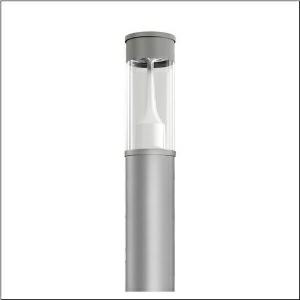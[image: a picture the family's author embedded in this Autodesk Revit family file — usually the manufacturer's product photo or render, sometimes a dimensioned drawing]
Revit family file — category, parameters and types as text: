
# Revit family: city-light_400_iq___p1_0a_5xa5305lf14hp_1a81
name_source: partatom
category: Lighting Fixtures
units: mm (PartAtom-declared; Revit-internal decimal feet)

## family parameters
Cut with Voids When Loaded = No
Host = Face
Light Source = No
Part Type = Normal
Room Calculation Point = No
Round Connector Dimension = Use Diameter
Shared = No

## types (1)
- --- (1 x LED, 4910 lm, 33.6 W, 4000K)
    Apparent Load = 34 VA
    CIE Flux Codes = 31 62 91 95 100
    Color Rendering = 70
    Color Temperature = 4000K
    Default Elevation = 1800 mm
    Description = City-Light 400 iQ, light pillar, Module 540 iQ-SR, primary light control with 3 zone facetted reflector, of plastic, silver coated, highly specular, structured, primary optical cover: cover, of PMMA, transparent, partly coated, light distribution: P1.0a, primary light characteristic: strongly asymmetric, LED, High Power LED, rated luminous flux: 4.910lm, luminous efficacy: 146lm/W, light colour: 740, colour temperature: 4000K, control gear: iQ Street-Remote, control: pre-setting: logarithmic dimming characteristic, Street-Remote, Auto-Match, Temp-Guard, Lumen-Switch, Night-Set, Smart-Wire, Light-Fading, Desk-Remote (wireless, voltage-free reading and setting of iQ features in the workshop via application-optimized NFC function/RFID function), optimised constant luminous flux control (CLO 2.0), with terminal, 6-pole, max. 2.5mm², mains connection: 230..240V, AC, 50/60Hz, start of lifetime: 34W, end of service life: 36W, reduction: 15W, luminaire housing, cylindrical, of extruded aluminium section, coated, Siteco® metallic grey (DB 702S), length: 4.694mm, diameter: 200mm, Module 540 iQ-SR, traffic white (RAL 9016), equipment: Power, protection rating (complete): IP65, insulation class (complete): insulation class II (safety insulation), certification: CE, ENEC, VDE, packaging unit: 1 piece

Light Distribution: P1.0a
    Height = 500 mm
    Lamp = 1 x LED
    Lamp Light Flux = 4910 lm
    Lamp Power = 33.6 W
    Lamp count = 1
    Length = 200 mm  [stored 0.656168 ft]
    Luminous efficacy = 146 lm/W
    Manufacturer = Siteco
    ModVariant = No
    Model = 5XA5305LF14HP
    Mounting Place = Floor
    Mounting Type = Freestanding
    Number of Poles = 1
    OnlyDefault = Yes
    Power Factor = 1
    Product Name = City-Light 400 iQ | P1.0a
    Product group = light pillar
    ProductGroupID = 1301
    Protection Class = Protection class II
    Protection Degree = IP 65
    RLX_Detail_Level = 1
    RLX_Emergency_Light_Flux = 0 lm
    RLX_Emergency_Type = 0
    RLX_Emergency_Type_DB = No
    RlxData = <blob elided: 53621 chars, md5=0aa2c980>
    Socket = socket
    Standby Power = 0 W
    System Light Flux = 4910 lm
    System Power = 34 W
    Type Comments = factory setting: luminous flux: 100 % | dim-lin: 254 | 695 mA
    Type Image = l_1006916.jpg
    URL = http://relux.com
    VarID = @adj_190173
    Voltage = 0 V
    Weight = 0.00 kg
    Width = 0 mm  [stored 0 ft]

note: [stored X ft] marks values corroborated as IEEE doubles in the binary element streams (Revit-internal decimal feet)

## geometry (parser evidence)
native form markers: Blend x4, Sweep x13
no freeform markers — native parametric forms only
